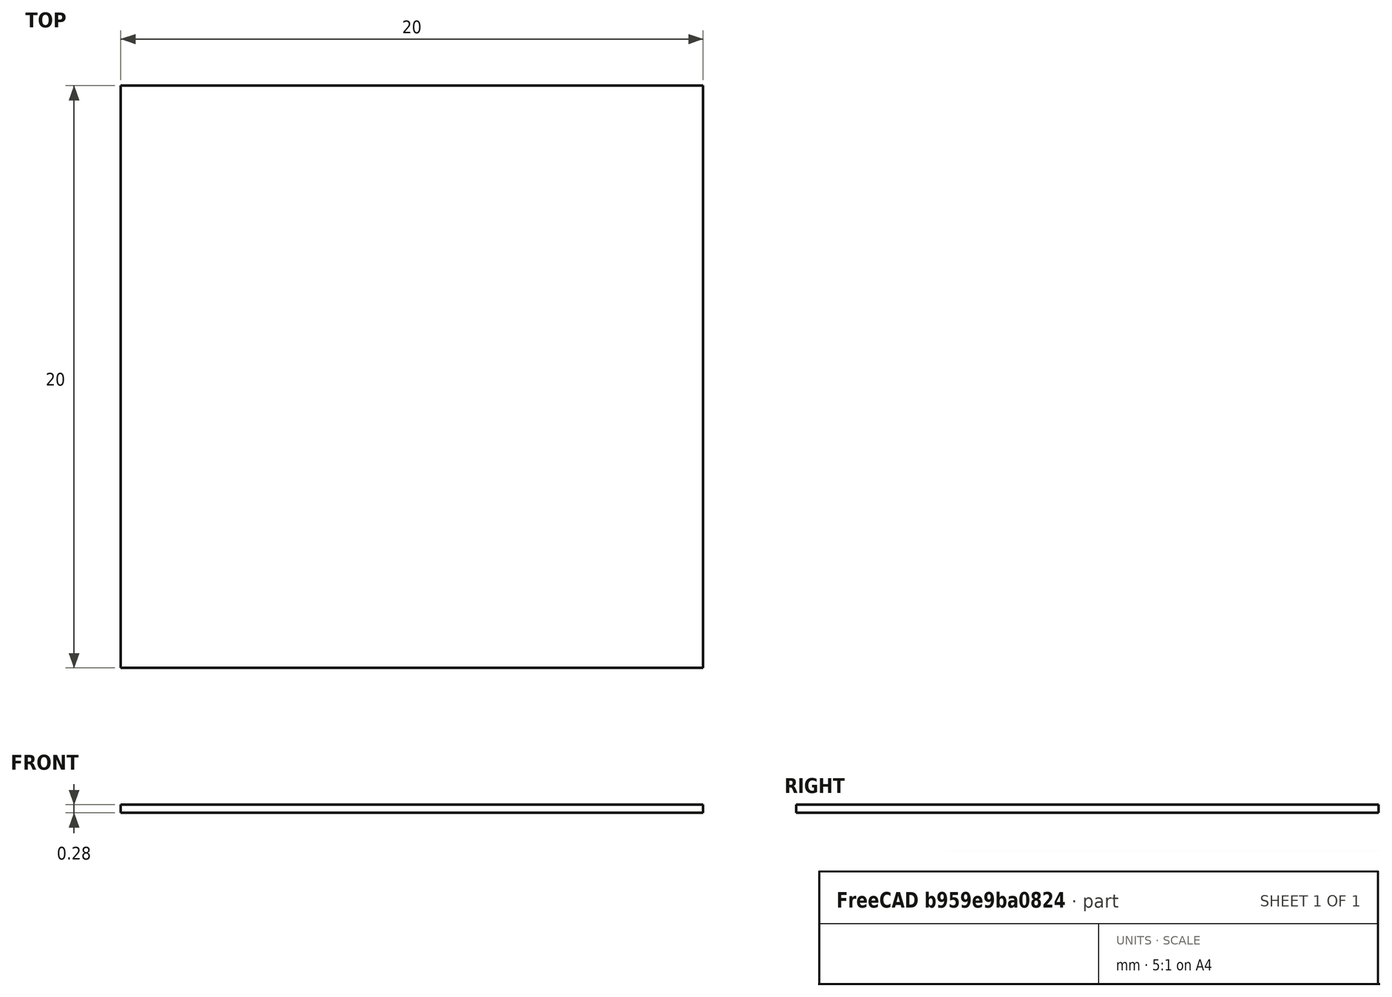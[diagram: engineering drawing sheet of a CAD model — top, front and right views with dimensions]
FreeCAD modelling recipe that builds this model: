
FCSTD DOCUMENT  (FreeCAD 0.18.4R)
Label: Sample_Holder_KIDS_Dummy
License: All rights reserved
LicenseURL: http://en.wikipedia.org/wiki/All_rights_reserved
objects: Sketcher::SketchObject×1, PartDesign::Pad×1, PartDesign::Body×1
note: 4 computed .brp shape members not serialized (recipe doc carries the construction recipe); baked Part::Feature solids carry a one-line shape summary decoded from their .brp

FEATURE [Sketcher::SketchObject] Sketch
  MapMode = 5
  Support = -> [XY_Plane]
  sketch-geometry (4):
    g0: LineSegment StartX=-10 StartY=10 StartZ=0 EndX=10 EndY=10 EndZ=0
    g1: LineSegment StartX=10 StartY=10 StartZ=0 EndX=10 EndY=-10 EndZ=0
    g2: LineSegment StartX=10 StartY=-10 StartZ=0 EndX=-10 EndY=-10 EndZ=0
    g3: LineSegment StartX=-10 StartY=-10 StartZ=0 EndX=-10 EndY=10 EndZ=0
  constraints (12):
    c: Coincident(g0,g1)
    c: Coincident(g1,g2)
    c: Coincident(g2,g3)
    c: Coincident(g3,g0)
    c: Horizontal(g0)
    c: Horizontal(g2)
    c: Vertical(g1)
    c: Vertical(g3)
    c: DistanceY(g1,g1) = 20
    c: DistanceX(g0,g0) = 20
    c: DistanceX(g-1,g1) = 10
    c: DistanceY(g2,g-1) = 10
FEATURE [PartDesign::Pad] Pad
  Length = 0.28
  Length2 = 100
  Profile = -> Sketch
  Type = 0
FEATURE [PartDesign::Body] Body
  Group = -> [Sketch,Pad]
  Origin = -> Origin
  Tip = -> Pad
